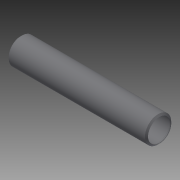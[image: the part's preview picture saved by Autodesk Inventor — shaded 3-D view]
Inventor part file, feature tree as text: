
AUTODESK INVENTOR PART (.ipt)
format: ipt  version: 2014 (Build 180170000, 170)  size: 121,856 bytes
history: native  units: in
note: dims shown in document units (in); Inventor stores cm internally (conversion verified against a paired STEP export)
features: other x56, revolve x1, sketch x1
ambient origin geometry x8: Origin, YZ Plane, XZ Plane, XY Plane, X Axis, Y Axis, Z Axis, Center Point
bodies: Solid1 (feature_tree)
feature tree (58):
  revolve  "Revolution1"  [1 undecoded]
  other  "o1_XY"
  other  "o1_YZ"
  other  "o1_ZX"
  other  "o1_X"
  other  "o1_Y"
  other  "o1_Z"
  other  "o1_Center"
  other  "o2_XY"
  other  "o2_YZ"
  other  "o2_ZX"
  other  "o2_X"
  other  "o2_Y"
  other  "o2_Z"
  other  "o2_Center"
  other  "t1_XY"
  other  "t1_YZ"
  other  "t1_ZX"
  other  "t1_X"
  other  "t1_Y"
  other  "t1_Z"
  other  "t1_Center"
  other  "t2_XY"
  other  "t2_YZ"
  other  "t2_ZX"
  other  "t2_X"
  other  "t2_Y"
  other  "t2_Z"
  other  "t2_Center"
  other  "t3_XY"
  other  "t3_YZ"
  other  "t3_ZX"
  other  "t3_X"
  other  "t3_Y"
  other  "t3_Z"
  other  "t3_Center"
  other  "t4_XY"
  other  "t4_YZ"
  other  "t4_ZX"
  other  "t4_X"
  other  "t4_Y"
  other  "t4_Z"
  other  "t4_Center"
  other  "tube1_XY"
  other  "tube1_YZ"
  other  "tube1_ZX"
  other  "tube1_X"
  other  "tube1_Y"
  other  "tube1_Z"
  other  "tube1_Center"
  other  "tube2_XY"
  other  "tube2_YZ"
  other  "tube2_ZX"
  other  "tube2_X"
  other  "tube2_Y"
  other  "tube2_Z"
  other  "tube2_Center"
  sketch  "Sketch_5"  dims[d0=360.0deg]
note: 1 required parameter value undecoded (feature->parameter linkage not recoverable at this tier; creation-order binding heuristic only, values carry confidence <= 0.55)
